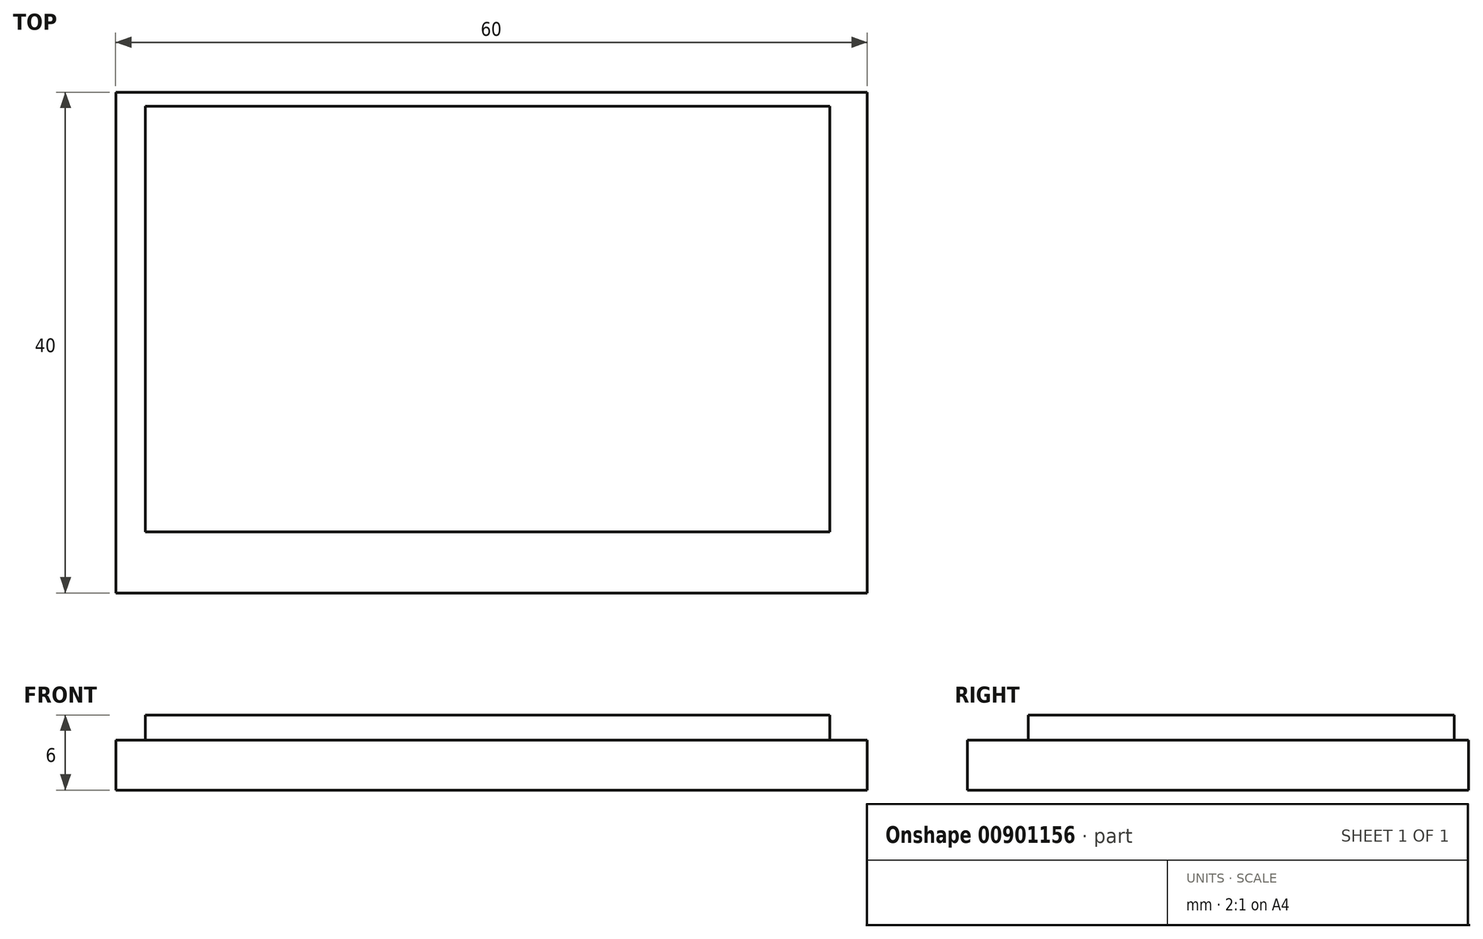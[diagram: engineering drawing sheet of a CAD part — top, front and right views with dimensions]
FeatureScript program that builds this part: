
annotation { "Feature Type Name" : "Feature", "Feature Type Description" : "" }
export const myFeature = defineFeature(function(context is Context, id is Id, definition is map)
    precondition{}
    {
        {
            var Q0;
            Q0=qCreatedBy(makeId("Top.planeOp"),FACE);
            var sketch = newSketch(context, id + "F0", { "sketchPlane" : qUnion([Q0])});
            skLineSegment(sketch, "E0.bottom", {"start": v(-34.98, 35.13) * mm, "end": v(25.02, 35.13) * mm});
            skLineSegment(sketch, "E0.top", {"start": v(-34.98, -4.87) * mm, "end": v(25.02, -4.87) * mm});
            skLineSegment(sketch, "E0.left", {"start": v(-34.98, 35.13) * mm, "end": v(-34.98, -4.87) * mm});
            skLineSegment(sketch, "E0.right", {"start": v(25.02, 35.13) * mm, "end": v(25.02, -4.87) * mm});
            skSolve(sketch);
        }
        {
            var Q0;
            Q0 = qSketchRegion(id + "F0", true);
            var Q1;
            Q1=makeQuery(id+"F0.imprint","IMPRINT",FACE,{"disambiguationData":[TD([[makeQuery(id+"F0.imprint","IMPRINT",EDGE,{"derivedFrom":sQuery(id+"F0.wireOp",EDGE,"E0.bottom")}),-1.0]])]});
            extrude(context, id + "F1", {"entities" : qUnion([Q0, Q1]), "depth" : 4 * mm, "offsetDistance" : 25 * mm});
        }
        {
            var Q0;
            Q0=makeQuery(id+"F1.opExtrude","CAP_FACE",FACE,{"disambiguationData":[OSD([sQuery(id+"F0.wireOp",EDGE,"E0.bottom"),sQuery(id+"F0.wireOp",EDGE,"E0.top"),sQuery(id+"F0.wireOp",EDGE,"E0.left"),sQuery(id+"F0.wireOp",EDGE,"E0.right")])],"isStart":false});
            var sketch = newSketch(context, id + "F2", { "sketchPlane" : qUnion([Q0])});
            skLineSegment(sketch, "E1.bottom", {"start": v(-32.61, 34) * mm, "end": v(22.02, 34) * mm});
            skLineSegment(sketch, "E1.top", {"start": v(-32.61, 0) * mm, "end": v(22.02, 0) * mm});
            skLineSegment(sketch, "E1.left", {"start": v(-32.61, 34) * mm, "end": v(-32.61, 0) * mm});
            skLineSegment(sketch, "E1.right", {"start": v(22.02, 34) * mm, "end": v(22.02, 0) * mm});
            skSolve(sketch);
        }
        {
            var Q0;
            Q0=makeQuery(id+"F2.imprint","IMPRINT",FACE,{"disambiguationData":[TD([[makeQuery(id+"F2.imprint","IMPRINT",EDGE,{"derivedFrom":sQuery(id+"F2.wireOp",EDGE,"E1.bottom")}),-1.0]])]});
            extrude(context, id + "F3", {"entities" : qUnion([Q0]), "operationType" : NewBodyOperationType.ADD, "depth" : 2 * mm, "offsetDistance" : 25 * mm});
        }
    });
